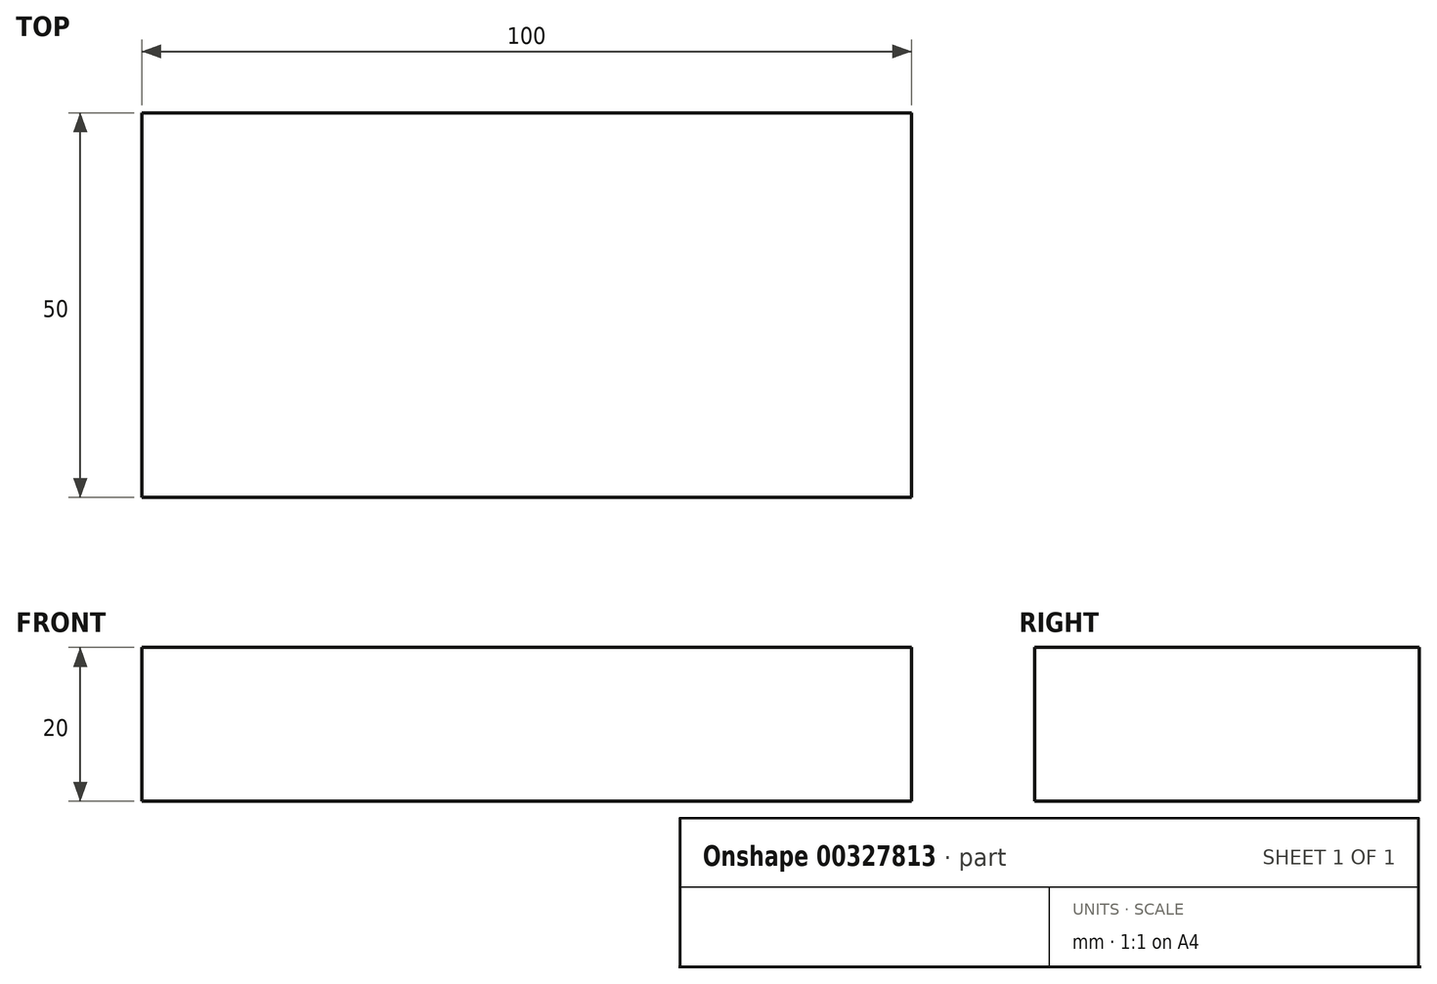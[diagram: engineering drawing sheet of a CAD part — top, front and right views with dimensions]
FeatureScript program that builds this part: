
annotation { "Feature Type Name" : "Feature", "Feature Type Description" : "" }
export const myFeature = defineFeature(function(context is Context, id is Id, definition is map)
    precondition{}
    {
        {
            var Q0;
            Q0=qCreatedBy(makeId("Top.planeOp"),FACE);
            var sketch = newSketch(context, id + "F0", { "sketchPlane" : qUnion([Q0])});
            skLineSegment(sketch, "E0.bottom", {"start": v(50, 25) * mm, "end": v(-50, 25) * mm});
            skLineSegment(sketch, "E0.top", {"start": v(50, -25) * mm, "end": v(-50, -25) * mm});
            skLineSegment(sketch, "E0.left", {"start": v(50, 25) * mm, "end": v(50, -25) * mm});
            skLineSegment(sketch, "E0.right", {"start": v(-50, 25) * mm, "end": v(-50, -25) * mm});
            skPoint(sketch, "E0.middle", {"position": v(0, 0) * mm});
            skSolve(sketch);
        }
        {
            var Q0;
            Q0=makeQuery(id+"F0.imprint","IMPRINT",FACE,{"disambiguationData":[TD([[makeQuery(id+"F0.imprint","IMPRINT",EDGE,{"derivedFrom":sQuery(id+"F0.wireOp",EDGE,"E0.bottom")}),1.0]])]});
            extrude(context, id + "F1", {"entities" : qUnion([Q0]), "depth" : 20 * mm});
        }
    });
